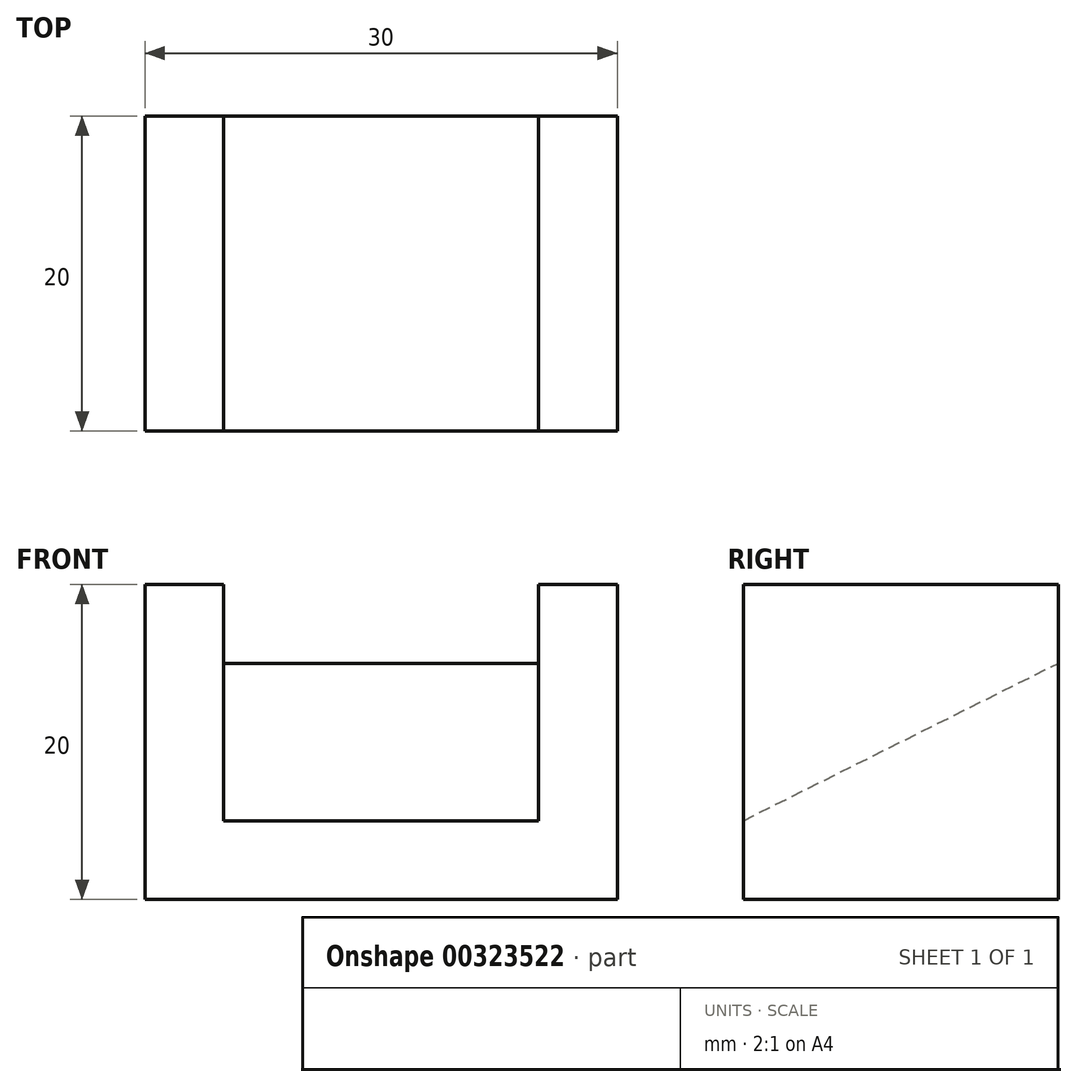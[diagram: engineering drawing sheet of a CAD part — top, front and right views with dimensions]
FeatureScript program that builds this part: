
annotation { "Feature Type Name" : "Feature", "Feature Type Description" : "" }
export const myFeature = defineFeature(function(context is Context, id is Id, definition is map)
    precondition{}
    {
        {
            var Q0;
            Q0=qCreatedBy(makeId("Front.planeOp"),FACE);
            var sketch = newSketch(context, id + "F0", { "sketchPlane" : qUnion([Q0])});
            skLineSegment(sketch, "E0", {"start": v(0, 0) * mm, "end": v(30, 0) * mm});
            skLineSegment(sketch, "E1", {"start": v(30, 0) * mm, "end": v(30, 20) * mm});
            skLineSegment(sketch, "E2", {"start": v(30, 20) * mm, "end": v(0, 20) * mm});
            skLineSegment(sketch, "E3", {"start": v(0, 20) * mm, "end": v(0, 0) * mm});
            skSolve(sketch);
        }
        {
            var Q0;
            Q0=makeQuery(id+"F0.imprint","IMPRINT",FACE,{"disambiguationData":[TD([[makeQuery(id+"F0.imprint","IMPRINT",EDGE,{"derivedFrom":sQuery(id+"F0.wireOp",EDGE,"E0")}),1.0]])]});
            extrude(context, id + "F1", {"entities" : qUnion([Q0]), "oppositeDirection" : true, "depth" : 20 * mm});
        }
        {
            var Q0;
            Q0=makeQuery(id+"F1.opExtrude","SWEPT_FACE",FACE,{"disambiguationData":[OSD([sQuery(id+"F0.wireOp",EDGE,"E1")])]});
            var sketch = newSketch(context, id + "F2", { "sketchPlane" : qUnion([Q0])});
            skLineSegment(sketch, "E4", {"start": v(0, 5) * mm, "end": v(20, 5) * mm});
            skLineSegment(sketch, "E5", {"start": v(20, 5) * mm, "end": v(20, 15) * mm});
            skLineSegment(sketch, "E6", {"start": v(20, 15) * mm, "end": v(0, 5) * mm});
            skSolve(sketch);
        }
        {
            var Q0;
            Q0=makeQuery(id+"F1.opExtrude","CAP_FACE",FACE,{"disambiguationData":[OSD([sQuery(id+"F0.wireOp",EDGE,"E0"),sQuery(id+"F0.wireOp",EDGE,"E1"),sQuery(id+"F0.wireOp",EDGE,"E2"),sQuery(id+"F0.wireOp",EDGE,"E3")])],"isStart":true});
            var sketch = newSketch(context, id + "F3", { "sketchPlane" : qUnion([Q0])});
            skLineSegment(sketch, "E7", {"start": v(0, 0) * mm, "end": v(30, 0) * mm});
            skLineSegment(sketch, "E8", {"start": v(30, 0) * mm, "end": v(30, 20) * mm});
            skLineSegment(sketch, "E9", {"start": v(30, 20) * mm, "end": v(25, 20) * mm});
            skLineSegment(sketch, "E10", {"start": v(25, 20) * mm, "end": v(25, 5) * mm});
            skLineSegment(sketch, "E11", {"start": v(25, 5) * mm, "end": v(5, 5) * mm});
            skLineSegment(sketch, "E12", {"start": v(5, 5) * mm, "end": v(5, 20) * mm});
            skLineSegment(sketch, "E13", {"start": v(5, 20) * mm, "end": v(0, 20) * mm});
            skLineSegment(sketch, "E14", {"start": v(0, 20) * mm, "end": v(0, 0) * mm});
            skSolve(sketch);
        }
        {
            var Q0;
            {var subQ0=sQuery(id+"F3.wireOp",EDGE,"E10");Q0=makeQuery(id+"F3.imprint","IMPRINT",FACE,{"disambiguationData":[TD([[makeQuery(id+"F3.imprint","IMPRINT",EDGE,{"derivedFrom":subQ0}),-1.0]])]});}
            extrude(context, id + "F4", {"entities" : qUnion([Q0]), "operationType" : NewBodyOperationType.REMOVE, "oppositeDirection" : true, "depth" : 25 * mm});
        }
        {
            var Q0;
            Q0=makeQuery(id+"F2.imprint","IMPRINT",FACE,{"disambiguationData":[TD([[makeQuery(id+"F2.imprint","IMPRINT",EDGE,{"derivedFrom":sQuery(id+"F2.wireOp",EDGE,"E4")}),1.0]])]});
            extrude(context, id + "F5", {"entities" : qUnion([Q0]), "operationType" : NewBodyOperationType.ADD, "oppositeDirection" : true, "depth" : 25 * mm});
        }
    });
